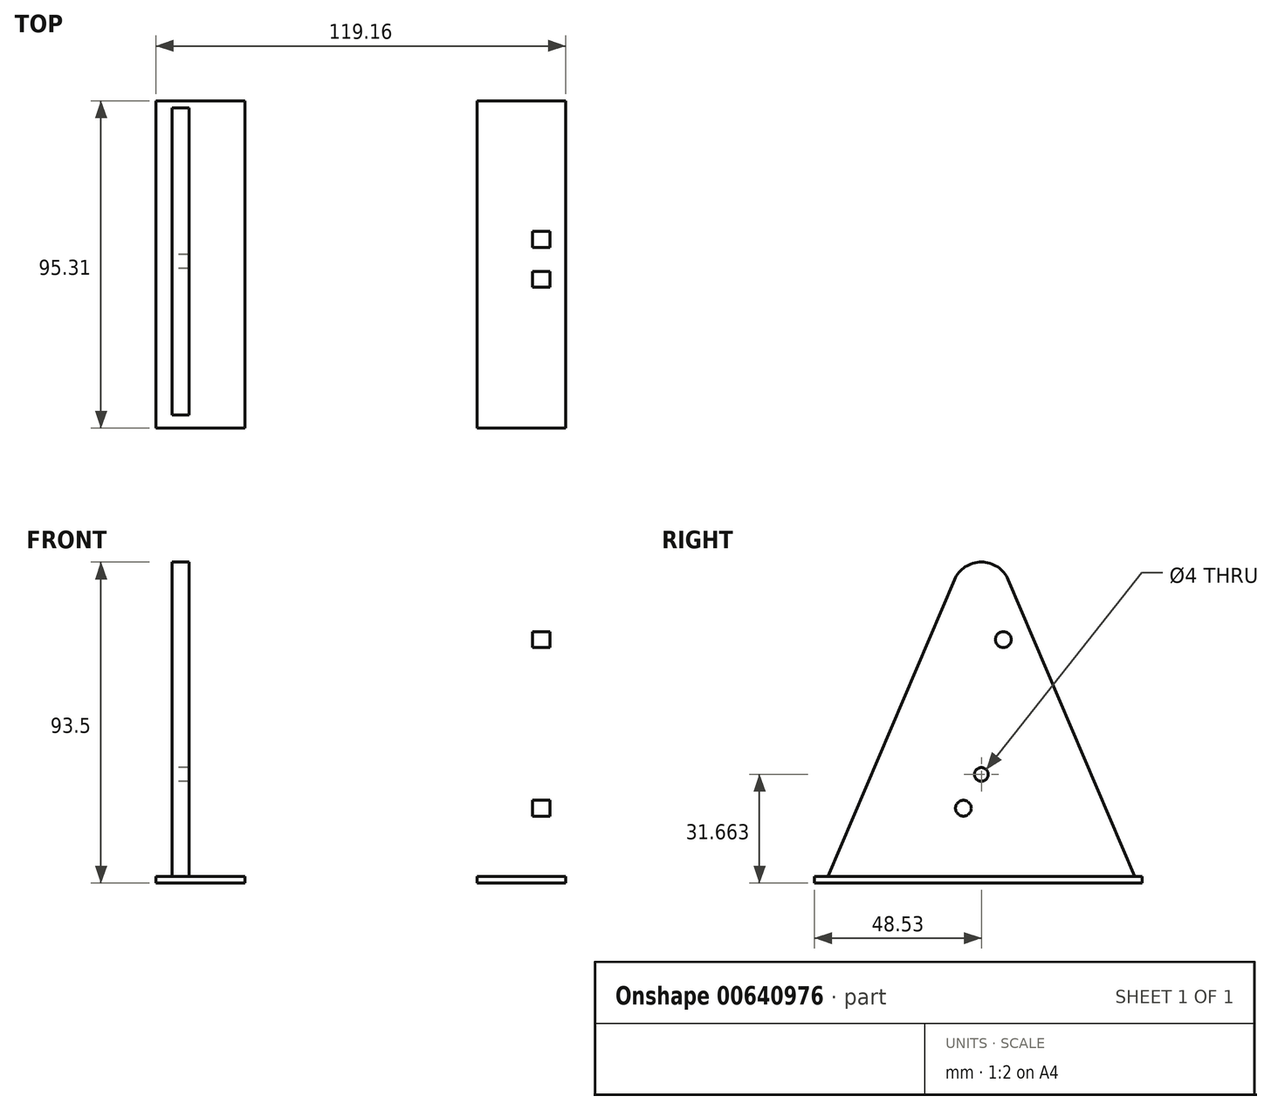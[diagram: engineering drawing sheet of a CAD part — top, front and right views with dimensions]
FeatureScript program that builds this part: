
annotation { "Feature Type Name" : "Feature", "Feature Type Description" : "" }
export const myFeature = defineFeature(function(context is Context, id is Id, definition is map)
    precondition{}
    {
        {
            var Q0;
            Q0=qCreatedBy(makeId("Right.planeOp"),FACE);
            cPlane(context, id + "F0", {"entities" : qUnion([Q0]), "cplaneType" : CPlaneType.OFFSET, "offset" : 50 * mm, "width" : 152.4 * mm, "height" : 152.4 * mm});
        }
        {
            var Q0;
            Q0=qCreatedBy(id+"F0.planeOp",FACE);
            var sketch = newSketch(context, id + "F1", { "sketchPlane" : qUnion([Q0])});
            skArc(sketch, "E0", {"start": v(7.85, 42.37) * mm, "mid": v(0, 47.56) * mm, "end": v(-7.85, 42.37) * mm});
            skLineSegment(sketch, "E1", {"start": v(0, -44.93) * mm, "end": v(45.09, -44.93) * mm});
            skLineSegment(sketch, "E2.MirrorCS", {"start": v(0, -44.93) * mm, "end": v(-45.08, -44.93) * mm});
            skLineSegment(sketch, "E3", {"start": v(45.09, -44.93) * mm, "end": v(7.85, 42.37) * mm});
            skLineSegment(sketch, "E4.MirrorCS", {"start": v(-45.09, -44.93) * mm, "end": v(-7.85, 42.37) * mm});
            skLineSegment(sketch, "E5.bottom", {"start": v(45.09, -44.93) * mm, "end": v(-45.09, -44.93) * mm});
            skLineSegment(sketch, "E5.top", {"start": v(45.08, -54.93) * mm, "end": v(-45.08, -54.93) * mm});
            skLineSegment(sketch, "E5.left", {"start": v(45.09, -44.93) * mm, "end": v(45.09, -54.93) * mm});
            skLineSegment(sketch, "E5.right", {"start": v(-45.08, -44.93) * mm, "end": v(-45.08, -54.93) * mm});
            skLineSegment(sketch, "E6", {"start": v(-48.46, -23.75) * mm, "end": v(49.2, -23.75) * mm, "construction": true});
            skSolve(sketch);
        }
        {
            var Q0;
            Q0=makeQuery(id+"F1.imprint","IMPRINT",FACE,{"disambiguationData":[TD([[makeQuery(id+"F1.imprint","IMPRINT",EDGE,{"derivedFrom":sQuery(id+"F1.wireOp",EDGE,"E0")}),1.0]])]});
            extrude(context, id + "F2", {"entities" : qUnion([Q0]), "depth" : 5 * mm, "offsetDistance" : 25.4 * mm});
        }
        {
            var Q0;
            Q0=qCreatedBy(makeId("Top.planeOp"),FACE);
            cPlane(context, id + "F3", {"entities" : qUnion([Q0]), "cplaneType" : CPlaneType.OFFSET, "offset" : 43.94 * mm, "oppositeDirection" : true, "width" : 152.4 * mm, "height" : 152.4 * mm});
        }
        {
            var Q0;
            Q0=makeQuery(id+"F2.opExtrude","SWEPT_BODY",BODY,{"disambiguationData":[OSD([sQuery(id+"F1.wireOp",EDGE,"E0"),sQuery(id+"F1.wireOp",EDGE,"E1"),sQuery(id+"F1.wireOp",EDGE,"E2.MirrorCS"),sQuery(id+"F1.wireOp",EDGE,"E3"),sQuery(id+"F1.wireOp",EDGE,"E4.MirrorCS")])]});
            var Q1;
            Q1=qCreatedBy(makeId("Right.planeOp"),FACE);
            mirror(context, id + "F4", {"entities" : qUnion([Q0]), "mirrorPlane" : qUnion([Q1])});
        }
        {
            var Q0;
            Q0=qCreatedBy(id+"F3.planeOp",FACE);
            var sketch = newSketch(context, id + "F5", { "sketchPlane" : qUnion([Q0])});
            skPoint(sketch, "E7.middle", {"position": v(-52.87, 0) * mm});
            skLineSegment(sketch, "E8.bottom", {"start": v(-59.58, 46.78) * mm, "end": v(-33.78, 46.78) * mm});
            skLineSegment(sketch, "E8.top", {"start": v(-59.58, -48.53) * mm, "end": v(-33.78, -48.53) * mm});
            skLineSegment(sketch, "E8.left", {"start": v(-59.58, 46.78) * mm, "end": v(-59.58, -48.53) * mm});
            skLineSegment(sketch, "E8.right", {"start": v(-33.78, 46.78) * mm, "end": v(-33.78, -48.53) * mm});
            skSolve(sketch);
        }
        {
            var Q0;
            Q0=makeQuery(id+"F5.imprint","IMPRINT",FACE,{"disambiguationData":[TD([[makeQuery(id+"F5.imprint","IMPRINT",EDGE,{"derivedFrom":sQuery(id+"F5.wireOp",EDGE,"E8.bottom")}),-1.0]])]});
            extrude(context, id + "F6", {"entities" : qUnion([Q0]), "operationType" : NewBodyOperationType.ADD, "oppositeDirection" : true, "depth" : 2 * mm, "offsetDistance" : 25.4 * mm});
        }
        {
            var Q0;
            Q0=makeQuery(id+"F4.opPattern","COPY",BODY,{"derivedFrom":makeQuery(id+"F2.opExtrude","SWEPT_BODY",BODY,{"disambiguationData":[OSD([sQuery(id+"F1.wireOp",EDGE,"E0"),sQuery(id+"F1.wireOp",EDGE,"E3"),sQuery(id+"F1.wireOp",EDGE,"E4.MirrorCS"),sQuery(id+"F1.wireOp",EDGE,"E5.bottom")])]}),"instanceName":"1"});
            var Q1;
            Q1=qCreatedBy(makeId("Right.planeOp"),FACE);
            mirror(context, id + "F7", {"operationType" : NewBodyOperationType.ADD, "entities" : qUnion([Q0]), "mirrorPlane" : qUnion([Q1])});
        }
        {
            var Q0;
            Q0=makeQuery(id+"F4.opPattern","COPY",FACE,{"derivedFrom":makeQuery(id+"F2.opExtrude","CAP_FACE",FACE,{"disambiguationData":[OSD([sQuery(id+"F1.wireOp",EDGE,"E0"),sQuery(id+"F1.wireOp",EDGE,"E3"),sQuery(id+"F1.wireOp",EDGE,"E4.MirrorCS"),sQuery(id+"F1.wireOp",EDGE,"E5.bottom")])],"isStart":false}),"instanceName":"1"});
            var sketch = newSketch(context, id + "F8", { "sketchPlane" : qUnion([Q0])});
            skPoint(sketch, "E9", {"position": v(0, -14.28) * mm});
            skSolve(sketch);
        }
        {
            var Q0;
            Q0=sQuery(id+"F8.wireOp",VERTEX,"E9");
            var Q1;
            Q1=makeQuery(id+"F4.opPattern","COPY",BODY,{"derivedFrom":makeQuery(id+"F2.opExtrude","SWEPT_BODY",BODY,{"disambiguationData":[OSD([sQuery(id+"F1.wireOp",EDGE,"E0"),sQuery(id+"F1.wireOp",EDGE,"E3"),sQuery(id+"F1.wireOp",EDGE,"E4.MirrorCS"),sQuery(id+"F1.wireOp",EDGE,"E5.bottom")])]}),"instanceName":"1"});
            hole(context, id + "F9", {"style" : HoleStyle.SIMPLE, "endStyle" : HoleEndStyle.BLIND, "holeDiameter" : 4 * mm, "majorDiameter" : 6.35 * mm, "holeDepth" : 15 * mm, "isTappedThrough" : true, "tappedDepth" : 12.7 * mm, "tapClearance" : 3, "locations" : qUnion([Q0]), "scope" : qUnion([Q1])});
        }
        {
            var Q0;
            Q0=makeQuery(id+"F2.opExtrude","CAP_FACE",FACE,{"disambiguationData":[OSD([sQuery(id+"F1.wireOp",EDGE,"E0"),sQuery(id+"F1.wireOp",EDGE,"E3"),sQuery(id+"F1.wireOp",EDGE,"E4.MirrorCS"),sQuery(id+"F1.wireOp",EDGE,"E5.bottom")])],"isStart":false});
            var sketch = newSketch(context, id + "F10", { "sketchPlane" : qUnion([Q0])});
            skPoint(sketch, "E10.middle", {"position": v(0.6, 24.2) * mm});
            skLineSegment(sketch, "E11.bottom", {"start": v(11.1, -20.56) * mm, "end": v(-9.9, -20.56) * mm});
            skLineSegment(sketch, "E11.top", {"start": v(11.1, 21.44) * mm, "end": v(-9.9, 21.44) * mm});
            skLineSegment(sketch, "E11.left", {"start": v(11.1, -20.56) * mm, "end": v(11.1, 21.44) * mm});
            skLineSegment(sketch, "E11.right", {"start": v(-9.9, -20.56) * mm, "end": v(-9.9, 21.44) * mm});
            skPoint(sketch, "E11.middle", {"position": v(0.6, 0.44) * mm});
            skCircle(sketch, "E12", {"center": v(-5.22, 24.99) * mm, "radius": 2.3 * mm});
            skCircle(sketch, "E13.MirrorC", {"center": v(6.4, 24.99) * mm, "radius": 2.3 * mm});
            skCircle(sketch, "E14.MirrorC", {"center": v(-5.22, -24.11) * mm, "radius": 2.3 * mm});
            skCircle(sketch, "E15.MirrorC", {"center": v(6.4, -24.11) * mm, "radius": 2.3 * mm});
            skSolve(sketch);
        }
        {
            var Q0;
            Q0=makeQuery(id+"F10.imprint","IMPRINT",FACE,{"disambiguationData":[TD([[makeQuery(id+"F10.imprint","IMPRINT",EDGE,{"derivedFrom":sQuery(id+"F10.wireOp",EDGE,"E11.bottom")}),-1.0]])]});
            var Q1;
            Q1=makeQuery(id+"F10.imprint","IMPRINT",FACE,{"disambiguationData":[TD([[makeQuery(id+"F10.imprint","IMPRINT",EDGE,{"derivedFrom":sQuery(id+"F10.wireOp",EDGE,"E12")}),1.0]])]});
            var Q2;
            Q2=makeQuery(id+"F10.imprint","IMPRINT",FACE,{"disambiguationData":[TD([[makeQuery(id+"F10.imprint","IMPRINT",EDGE,{"derivedFrom":sQuery(id+"F10.wireOp",EDGE,"E13.MirrorC")}),-1.0]])]});
            var Q3;
            Q3=makeQuery(id+"F10.imprint","IMPRINT",FACE,{"disambiguationData":[TD([[makeQuery(id+"F10.imprint","IMPRINT",EDGE,{"derivedFrom":sQuery(id+"F10.wireOp",EDGE,"E14.MirrorC")}),-1.0]])]});
            var Q4;
            Q4=makeQuery(id+"F10.imprint","IMPRINT",FACE,{"disambiguationData":[TD([[makeQuery(id+"F10.imprint","IMPRINT",EDGE,{"derivedFrom":sQuery(id+"F10.wireOp",EDGE,"E15.MirrorC")}),1.0]])]});
            extrude(context, id + "F11", {"entities" : qUnion([Q0, Q1, Q2, Q3, Q4]), "operationType" : NewBodyOperationType.REMOVE, "oppositeDirection" : true, "depth" : 6 * mm, "offsetDistance" : 25.4 * mm});
        }
    });
